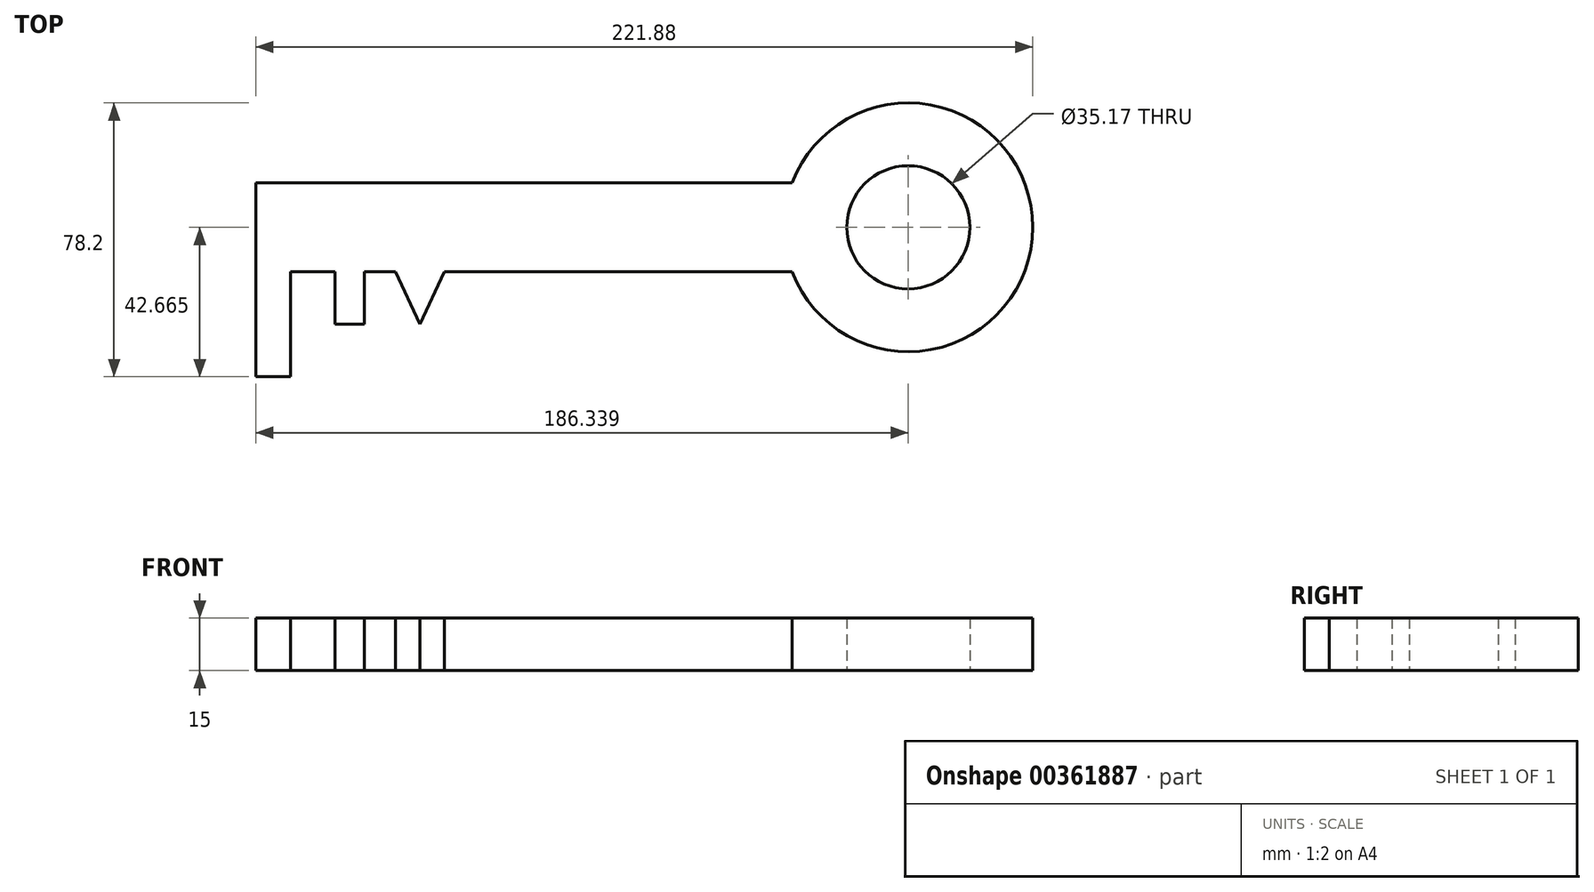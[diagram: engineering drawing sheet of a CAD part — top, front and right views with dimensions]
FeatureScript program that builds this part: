
annotation { "Feature Type Name" : "Feature", "Feature Type Description" : "" }
export const myFeature = defineFeature(function(context is Context, id is Id, definition is map)
    precondition{}
    {
        {
            var Q0;
            Q0=qCreatedBy(makeId("Top.planeOp"),FACE);
            var sketch = newSketch(context, id + "F0", { "sketchPlane" : qUnion([Q0])});
            skLineSegment(sketch, "E0.bottom", {"start": v(79.2, 25.4) * mm, "end": v(-73.95, 25.4) * mm});
            skLineSegment(sketch, "E0.top", {"start": v(79.2, 0) * mm, "end": v(-73.95, 0) * mm});
            skLineSegment(sketch, "E0.right", {"start": v(-73.95, 25.4) * mm, "end": v(-73.95, 0) * mm});
            skLineSegment(sketch, "E1.bottom", {"start": v(-73.95, 0) * mm, "end": v(-73.95, 0) * mm});
            skLineSegment(sketch, "E1.top", {"start": v(-73.95, -29.97) * mm, "end": v(-73.95, -29.97) * mm});
            skLineSegment(sketch, "E1.left", {"start": v(-73.95, 0) * mm, "end": v(-73.95, -29.97) * mm});
            skLineSegment(sketch, "E1.right", {"start": v(-73.95, 0) * mm, "end": v(-73.95, -29.97) * mm});
            skLineSegment(sketch, "E2.bottom", {"start": v(-63.42, -29.97) * mm, "end": v(-64.02, -29.97) * mm});
            skLineSegment(sketch, "E2.top", {"start": v(-63.42, 0) * mm, "end": v(-64.02, 0) * mm});
            skLineSegment(sketch, "E2.left", {"start": v(-64.02, -29.97) * mm, "end": v(-64.02, 0) * mm});
            skLineSegment(sketch, "E3.bottom", {"start": v(-63.42, -29.97) * mm, "end": v(-73.95, -29.97) * mm});
            skLineSegment(sketch, "E3.top", {"start": v(-63.42, -29.97) * mm, "end": v(-73.95, -29.97) * mm});
            skLineSegment(sketch, "E3.left", {"start": v(-63.42, -29.97) * mm, "end": v(-63.42, -29.97) * mm});
            skLineSegment(sketch, "E4.bottom", {"start": v(-51.08, 0) * mm, "end": v(-51.38, 0) * mm});
            skLineSegment(sketch, "E4.top", {"start": v(-51.08, -14.92) * mm, "end": v(-51.38, -14.92) * mm});
            skLineSegment(sketch, "E4.left", {"start": v(-51.08, 0) * mm, "end": v(-51.08, -14.92) * mm});
            skLineSegment(sketch, "E4.right", {"start": v(-51.38, 0) * mm, "end": v(-51.38, -14.92) * mm});
            skLineSegment(sketch, "E5.bottom", {"start": v(-42.96, -14.92) * mm, "end": v(-42.96, -14.92) * mm});
            skLineSegment(sketch, "E5.top", {"start": v(-42.96, 0) * mm, "end": v(-42.96, 0) * mm});
            skLineSegment(sketch, "E5.left", {"start": v(-42.96, -14.92) * mm, "end": v(-42.96, 0) * mm});
            skLineSegment(sketch, "E5.right", {"start": v(-42.96, -14.92) * mm, "end": v(-42.96, 0) * mm});
            skLineSegment(sketch, "E6.bottom", {"start": v(-51.08, -14.92) * mm, "end": v(-42.96, -14.92) * mm});
            skLineSegment(sketch, "E6.top", {"start": v(-51.08, -14.92) * mm, "end": v(-42.96, -14.92) * mm});
            skLineSegment(sketch, "E6.left", {"start": v(-51.08, -14.92) * mm, "end": v(-51.08, -14.92) * mm});
            skLineSegment(sketch, "E7", {"start": v(-34.13, 0) * mm, "end": v(-27.13, -15) * mm});
            skLineSegment(sketch, "E8", {"start": v(-27.13, -15) * mm, "end": v(-20.13, 0) * mm});
            skArc(sketch, "E9", {"start": v(79.2, 0) * mm, "mid": v(147.93, 12.7) * mm, "end": v(79.2, 25.4) * mm});
            skCircle(sketch, "E10", {"center": v(112.39, 12.7) * mm, "radius": 17.58 * mm});
            skSolve(sketch);
        }
        {
            var Q0;
            Q0 = qSketchRegion(id + "F0", true);
            extrude(context, id + "F1", {"entities" : qUnion([Q0]), "depth" : 15 * mm});
        }
    });
